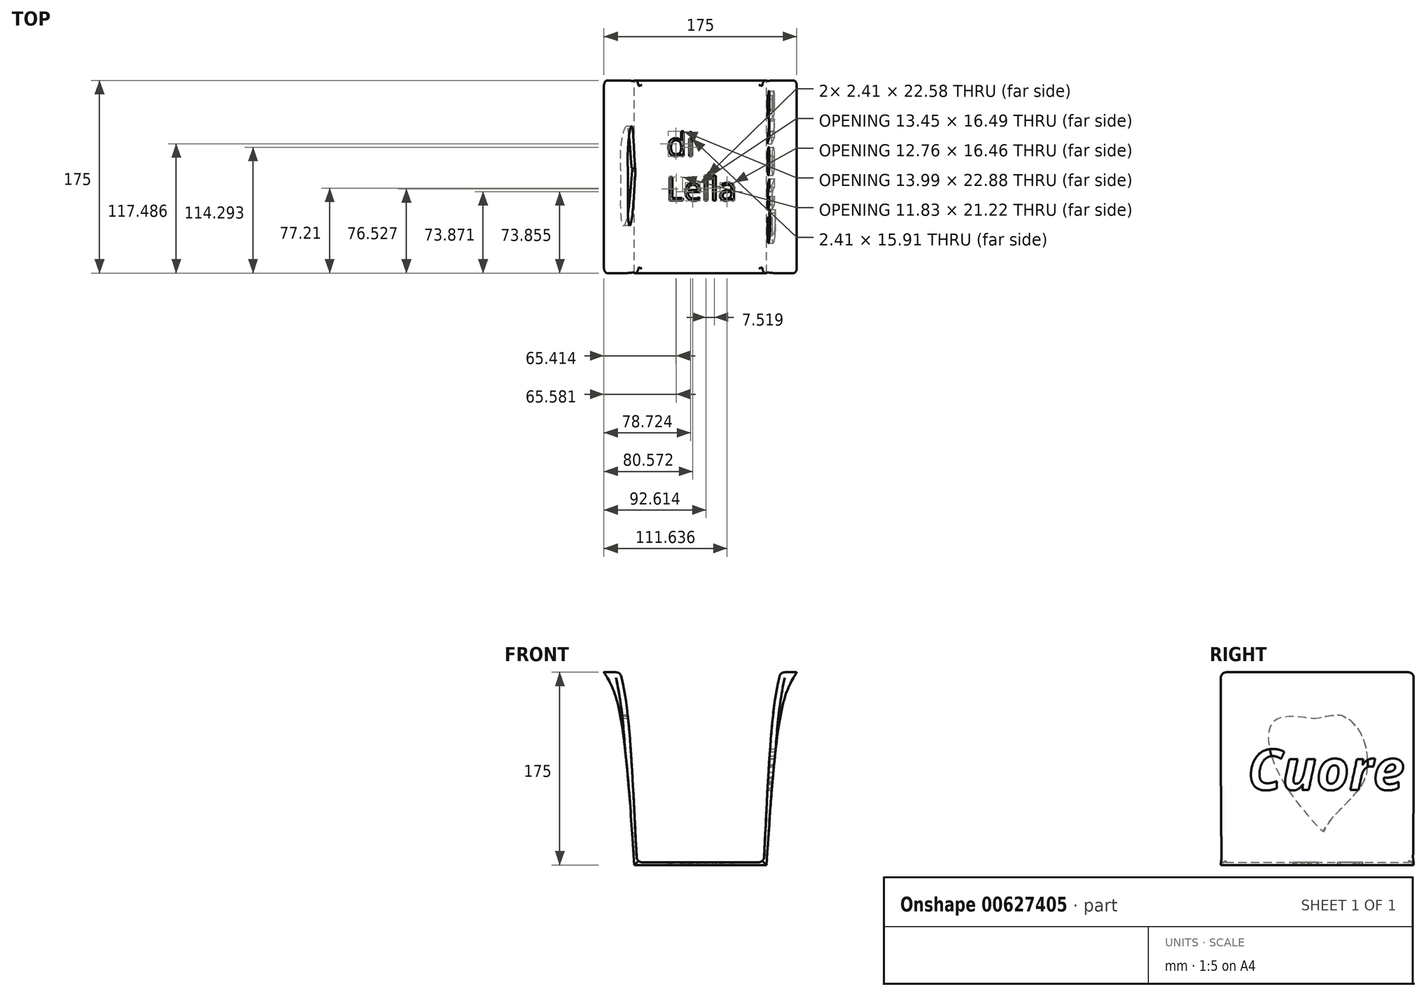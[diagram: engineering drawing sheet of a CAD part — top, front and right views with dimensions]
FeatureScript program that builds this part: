
annotation { "Feature Type Name" : "Feature", "Feature Type Description" : "" }
export const myFeature = defineFeature(function(context is Context, id is Id, definition is map)
    precondition{}
    {
        {
            var Q0;
            Q0=qCreatedBy(makeId("Front.planeOp"),FACE);
            var sketch = newSketch(context, id + "F0", { "sketchPlane" : qUnion([Q0])});
            skLineSegment(sketch, "E0", {"start": v(-60, -68.17) * mm, "end": v(0, -68.17) * mm});
            skLineSegment(sketch, "E1", {"start": v(0, 136.89) * mm, "end": v(0, -156.21) * mm, "construction": true});
            skLineSegment(sketch, "E2.MirrorCS", {"start": v(60, -68.17) * mm, "end": v(0, -68.17) * mm});
            skPoint(sketch, "E3.end.orphan", {"position": v(87.5, 106.83) * mm});
            skPoint(sketch, "E3.start.orphan", {"position": v(0, 106.83) * mm});
            skPoint(sketch, "E4.MirrorCS.end.orphan", {"position": v(-87.5, 106.83) * mm});
            skLineSegment(sketch, "E5", {"start": v(-87.5, 106.83) * mm, "end": v(87.5, 106.83) * mm, "construction": true});
            skLineSegment(sketch, "E6", {"start": v(87.5, 106.83) * mm, "end": v(60, -68.17) * mm, "construction": true});
            skLineSegment(sketch, "E7", {"start": v(60, -68.17) * mm, "end": v(60, 133.84) * mm, "construction": true});
            skFitSpline(sketch, "E8", {"points": [v(87.5, 106.83) * mm, v(75.74, 80.97) * mm, v(60, -68.17) * mm], "startDerivative": vector(-41.26, -65.74) * mm, "endDerivative": vector(-16.93, -258.92) * mm});
            skFitSpline(sketch, "E9.MirrorCS", {"points": [v(-87.5, 106.83) * mm, v(-75.74, 80.97) * mm, v(-60, -68.17) * mm], "startDerivative": vector(41.26, -65.74) * mm, "endDerivative": vector(16.93, -258.92) * mm});
            skLineSegment(sketch, "E10", {"start": v(87.5, 106.83) * mm, "end": v(72.5, 106.83) * mm});
            skLineSegment(sketch, "E11.0", {"start": v(53.93, -65.67) * mm, "end": v(0, -65.67) * mm});
            skLineSegment(sketch, "E12.0", {"start": v(-60, -65.67) * mm, "end": v(0, -65.67) * mm});
            skPoint(sketch, "E13.start.orphan", {"position": v(53.93, -65.67) * mm});
            skLineSegment(sketch, "E14", {"start": v(53.93, -65.67) * mm, "end": v(60.16, -65.67) * mm});
            skLineSegment(sketch, "E15", {"start": v(57.66, -65.67) * mm, "end": v(60.16, -65.67) * mm});
            skFitSpline(sketch, "E16", {"points": [v(72.5, 106.83) * mm, v(66.26, 70.66) * mm, v(57.66, -65.67) * mm], "startDerivative": vector(-19.17, -88.7) * mm, "endDerivative": vector(-11.33, -240.28) * mm});
            skFitSpline(sketch, "E17.MirrorCS", {"points": [v(-72.5, 106.83) * mm, v(-66.26, 70.66) * mm, v(-57.66, -65.67) * mm], "startDerivative": vector(19.17, -88.7) * mm, "endDerivative": vector(11.33, -240.28) * mm});
            skLineSegment(sketch, "E18.MirrorCS", {"start": v(-87.5, 106.83) * mm, "end": v(-72.5, 106.83) * mm});
            skSolve(sketch);
        }
        {
            var Q0;
            {var subQ0=sQuery(id+"F0.wireOp",EDGE,"E10");Q0=makeQuery(id+"F0.imprint","IMPRINT",FACE,{"disambiguationData":[TD([[makeQuery(id+"F0.imprint","IMPRINT",EDGE,{"derivedFrom":subQ0}),1.0]])]});}
            var Q1;
            Q1=makeQuery(id+"F0.imprint","IMPRINT",FACE,{"disambiguationData":[TD([[makeQuery(id+"F0.imprint","IMPRINT",EDGE,{"derivedFrom":sQuery(id+"F0.wireOp",EDGE,"E0")}),1.0]])]});
            extrude(context, id + "F1", {"entities" : qUnion([Q0, Q1]), "depth" : 175 * mm, "offsetDistance" : 25 * mm});
        }
        {
            var Q0;
            Q0=makeQuery(id+"F1.opExtrude","SWEPT_EDGE",EDGE,{"disambiguationData":[OSD([sQuery(id+"F0.wireOp",EDGE,"E17.MirrorCS"),sQuery(id+"F0.wireOp",EDGE,"E18.MirrorCS")])]});
            var Q1;
            Q1=makeQuery(id+"F1.opExtrude","SWEPT_EDGE",EDGE,{"disambiguationData":[OSD([sQuery(id+"F0.wireOp",EDGE,"E10"),sQuery(id+"F0.wireOp",EDGE,"E16")])]});
            var Q2;
            Q2=makeQuery(id+"F1.opExtrude","SWEPT_EDGE",EDGE,{"disambiguationData":[OSD([sQuery(id+"F0.wireOp",EDGE,"E12.0"),sQuery(id+"F0.wireOp",EDGE,"E17.MirrorCS")])]});
            var Q3;
            Q3=makeQuery(id+"F1.opExtrude","SWEPT_EDGE",EDGE,{"disambiguationData":[OSD([sQuery(id+"F0.wireOp",EDGE,"E14"),sQuery(id+"F0.wireOp",EDGE,"E15"),sQuery(id+"F0.wireOp",EDGE,"E16")])]});
            fillet(context, id + "F2", {"entities" : qUnion([Q0, Q1, Q2, Q3]), "radius" : 5 * mm, "tangentPropagation" : true, "allowEdgeOverflow" : false});
        }
        {
            var Q0;
            Q0=qCreatedBy(makeId("Right.planeOp"),FACE);
            cPlane(context, id + "F3", {"entities" : qUnion([Q0]), "cplaneType" : CPlaneType.OFFSET, "offset" : 80 * mm, "width" : 150 * mm, "height" : 150 * mm});
        }
        {
            var Q0;
            Q0=qCreatedBy(id+"F3.planeOp",FACE);
            var sketch = newSketch(context, id + "F4", { "sketchPlane" : qUnion([Q0])});
            skText(sketch, "E19", { "text": "Cuore\n", "fontName": "OpenSans-BoldItalic.ttf"});
            const initialGuessF4  = {"E19": [-0.15076, 0, 1, 0, 0.0369]};
            skSetInitialGuess(sketch, initialGuessF4);
            skSolve(sketch);
        }
        {
            var Q0;
            Q0=makeQuery(id+"F4.imprint","IMPRINT",FACE,{"disambiguationData":[TD([[makeQuery(id+"F4.imprint","IMPRINT",EDGE,{"derivedFrom":sQuery(id+"F4.wireOp",EDGE,"E19.sketch_text.stroke-53")}),-1.0]])]});
            var Q1;
            Q1=makeQuery(id+"F4.imprint","IMPRINT",FACE,{"disambiguationData":[TD([[makeQuery(id+"F4.imprint","IMPRINT",EDGE,{"derivedFrom":sQuery(id+"F4.wireOp",EDGE,"E19.sketch_text.stroke-0")}),-1.0]])]});
            var Q2;
            Q2=makeQuery(id+"F4.imprint","IMPRINT",FACE,{"disambiguationData":[TD([[makeQuery(id+"F4.imprint","IMPRINT",EDGE,{"derivedFrom":sQuery(id+"F4.wireOp",EDGE,"E19.sketch_text.stroke-18")}),-1.0]])]});
            var Q3;
            Q3=makeQuery(id+"F4.imprint","IMPRINT",FACE,{"disambiguationData":[TD([[makeQuery(id+"F4.imprint","IMPRINT",EDGE,{"derivedFrom":sQuery(id+"F4.wireOp",EDGE,"E19.sketch_text.stroke-35")}),-1.0]])]});
            var Q4;
            Q4=makeQuery(id+"F4.imprint","IMPRINT",FACE,{"disambiguationData":[TD([[makeQuery(id+"F4.imprint","IMPRINT",EDGE,{"derivedFrom":sQuery(id+"F4.wireOp",EDGE,"E19.sketch_text.stroke-65")}),-1.0]])]});
            extrude(context, id + "F5", {"entities" : qUnion([Q0, Q1, Q2, Q3, Q4]), "operationType" : NewBodyOperationType.REMOVE, "oppositeDirection" : true, "depth" : 25 * mm, "offsetDistance" : 25 * mm});
        }
        {
            var Q0;
            Q0=qCreatedBy(makeId("Right.planeOp"),FACE);
            cPlane(context, id + "F6", {"entities" : qUnion([Q0]), "cplaneType" : CPlaneType.OFFSET, "offset" : 150 * mm, "oppositeDirection" : true, "width" : 150 * mm, "height" : 150 * mm});
        }
        {
            var Q0;
            Q0=qCreatedBy(id+"F6.planeOp",FACE);
            var sketch = newSketch(context, id + "F7", { "sketchPlane" : qUnion([Q0])});
            skFitSpline(sketch, "E20", {"points": [v(-85.99, 65.1) * mm, v(-66.98, 67.76) * mm, v(-48.18, 52.03) * mm, v(-41.64, 24.24) * mm, v(-50.02, 0) * mm, v(-79.85, -35.03) * mm, v(-79.65, -39.52) * mm, v(-119.7, 9.52) * mm, v(-127.47, 61.63) * mm, v(-102.74, 66.13) * mm, v(-85.99, 65.1) * mm]});
            skSolve(sketch);
        }
        {
            var Q0;
            Q0=makeQuery(id+"F7.imprint","IMPRINT",FACE,{"disambiguationData":[TD([[makeQuery(id+"F7.imprint","IMPRINT",EDGE,{"derivedFrom":sQuery(id+"F7.wireOp",EDGE,"E20")}),-1.0]])]});
            extrude(context, id + "F8", {"entities" : qUnion([Q0]), "operationType" : NewBodyOperationType.REMOVE, "depth" : 100 * mm, "offsetDistance" : 25 * mm});
        }
        {
            var Q0;
            Q0=makeQuery(id+"F1.opExtrude","SWEPT_FACE",FACE,{"disambiguationData":[OSD([sQuery(id+"F0.wireOp",EDGE,"E11.0"),sQuery(id+"F0.wireOp",EDGE,"E12.0"),sQuery(id+"F0.wireOp",EDGE,"E14")])]});
            var sketch = newSketch(context, id + "F9", { "sketchPlane" : qUnion([Q0])});
            skText(sketch, "E21", { "text": "di\nLella", "fontName": "OpenSans-Regular.ttf"});
            const initialGuessF9  = {"E21": [-0.03075, -0.06866, 1, 0, 0.0214]};
            skSetInitialGuess(sketch, initialGuessF9);
            skSolve(sketch);
        }
        {
            var Q0;
            Q0=makeQuery(id+"F9.imprint","IMPRINT",FACE,{"disambiguationData":[TD([[makeQuery(id+"F9.imprint","IMPRINT",EDGE,{"derivedFrom":sQuery(id+"F9.wireOp",EDGE,"E21.sketch_text.stroke-65")}),-1.0]])]});
            var Q1;
            Q1 = qSketchRegion(id + "F9", true);
            var Q2;
            Q2=makeQuery(id+"F9.imprint","IMPRINT",FACE,{"disambiguationData":[TD([[makeQuery(id+"F9.imprint","IMPRINT",EDGE,{"derivedFrom":sQuery(id+"F9.wireOp",EDGE,"E21.sketch_text.stroke-36")}),-1.0]])]});
            var Q3;
            Q3=makeQuery(id+"F9.imprint","IMPRINT",FACE,{"disambiguationData":[TD([[makeQuery(id+"F9.imprint","IMPRINT",EDGE,{"derivedFrom":sQuery(id+"F9.wireOp",EDGE,"E21.sketch_text.stroke-69")}),-1.0]])]});
            var Q4;
            Q4=makeQuery(id+"F9.imprint","IMPRINT",FACE,{"disambiguationData":[TD([[makeQuery(id+"F9.imprint","IMPRINT",EDGE,{"derivedFrom":sQuery(id+"F9.wireOp",EDGE,"E21.sketch_text.stroke-61")}),-1.0]])]});
            var Q5;
            Q5=makeQuery(id+"F9.imprint","IMPRINT",FACE,{"disambiguationData":[TD([[makeQuery(id+"F9.imprint","IMPRINT",EDGE,{"derivedFrom":sQuery(id+"F9.wireOp",EDGE,"E21.sketch_text.stroke-42")}),-1.0]])]});
            var Q6;
            Q6=makeQuery(id+"F9.imprint","IMPRINT",FACE,{"disambiguationData":[TD([[makeQuery(id+"F9.imprint","IMPRINT",EDGE,{"derivedFrom":sQuery(id+"F9.wireOp",EDGE,"E21.sketch_text.stroke-28")}),-1.0]])]});
            var Q7;
            Q7=makeQuery(id+"F9.imprint","IMPRINT",FACE,{"disambiguationData":[TD([[makeQuery(id+"F9.imprint","IMPRINT",EDGE,{"derivedFrom":sQuery(id+"F9.wireOp",EDGE,"E21.sketch_text.stroke-0")}),-1.0]])]});
            var Q8;
            Q8=makeQuery(id+"F9.imprint","IMPRINT",FACE,{"disambiguationData":[TD([[makeQuery(id+"F9.imprint","IMPRINT",EDGE,{"derivedFrom":sQuery(id+"F9.wireOp",EDGE,"E21.sketch_text.stroke-24")}),-1.0]])]});
            extrude(context, id + "F10", {"entities" : qUnion([Q0, Q1, Q2, Q3, Q4, Q5, Q6, Q7, Q8]), "operationType" : NewBodyOperationType.REMOVE, "oppositeDirection" : true, "depth" : 25 * mm, "offsetDistance" : 25 * mm});
        }
        {
            var Q0;
            Q0=makeQuery(id+"F1.opExtrude","CAP_EDGE",EDGE,{"disambiguationData":[OSD([sQuery(id+"F0.wireOp",EDGE,"E11.0"),sQuery(id+"F0.wireOp",EDGE,"E12.0"),sQuery(id+"F0.wireOp",EDGE,"E14")])],"isStart":false});
            var Q1;
            Q1=makeQuery(id+"F1.opExtrude","CAP_EDGE",EDGE,{"disambiguationData":[OSD([sQuery(id+"F0.wireOp",EDGE,"E16")])],"isStart":true});
            fillet(context, id + "F11", {"entities" : qUnion([Q0, Q1]), "radius" : 5 * mm, "tangentPropagation" : true, "allowEdgeOverflow" : false});
        }
    });
